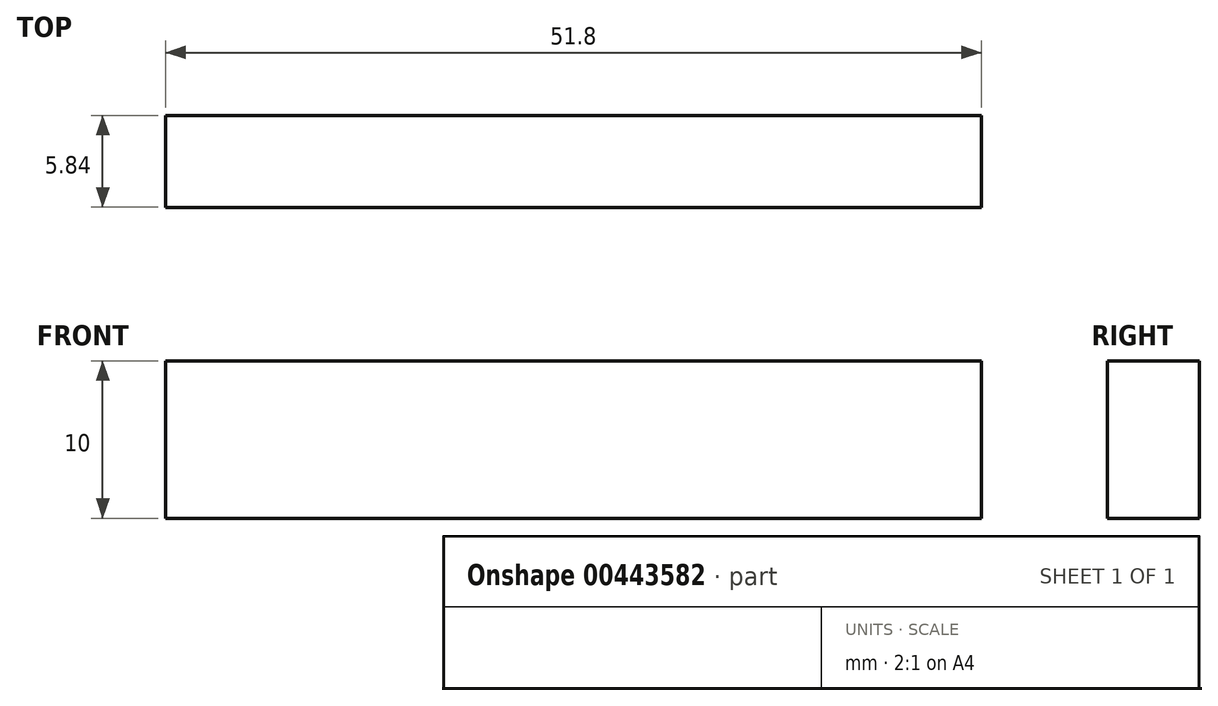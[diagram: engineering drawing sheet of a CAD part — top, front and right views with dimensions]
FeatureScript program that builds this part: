
annotation { "Feature Type Name" : "Feature", "Feature Type Description" : "" }
export const myFeature = defineFeature(function(context is Context, id is Id, definition is map)
    precondition{}
    {
        {
            var Q0;
            Q0=qCreatedBy(makeId("Front.planeOp"),FACE);
            var sketch = newSketch(context, id + "F0", { "sketchPlane" : qUnion([Q0])});
            skLineSegment(sketch, "E0.bottom", {"start": v(0, 0) * mm, "end": v(51.8, 0) * mm});
            skLineSegment(sketch, "E0.top", {"start": v(0, 10) * mm, "end": v(51.8, 10) * mm});
            skLineSegment(sketch, "E0.left", {"start": v(0, 0) * mm, "end": v(0, 10) * mm});
            skLineSegment(sketch, "E0.right", {"start": v(51.8, 0) * mm, "end": v(51.8, 10) * mm});
            skSolve(sketch);
        }
        {
            var Q0;
            Q0 = qSketchRegion(id + "F0", true);
            extrude(context, id + "F1", {"entities" : qUnion([Q0]), "depth" : 5.84 * mm});
        }
    });
